# Revit family: SENTINEL KINETIC PLUS_130510_Vent-Axia
name_source: partatom
category: Mechanical Equipment
revit_build: Autodesk Revit MEP 2013 (Build: 20120221_2030(x64)
units: mm (PartAtom-declared; Revit-internal decimal feet)

## types (1)
- Kinetic- B
    A = • Manufactured in the UK, • Building Regulations Part F compliant
    AC Frequency Input = 50Hz nominal
    AC Voltage Input = 220-240 V AC (single phase)
    Air Intake Temperature = (-20C to +45C)
    B = • SAP Appendix Q Eligible, • Energy savings trust best practice compliant
    C = • Up to 92% heat recovery whilst controlling condensation  Unique folding filter for removal when access is restricted
    Category = Sentinel Kinetic
    Cell Clearance = 430 mm
    Condensate Pipe Diameter = 22 mm  [stored 0.0721785 ft]
    Consultants Spec. = Operation
The supply and extract ventilation unit shall be as Sentinel Kinetic as manufactured by Vent-Axia and shall be sized as indicated on the drawings and shall be in accordance with the particular specification.
Supply air to the room shall be pre-heated by the extract air via the integrated composite plastic counterflow heat recovery cell. The Sentinel Kinetic shall automatically vary the ventilation rate via EC/DC motors, as it receives signals from one of the optional interconnected sensors. When a signal is received, the fans shall either vary their speed proportionally or on a trickle and boost principle. The unit shall have the facility to commission the supply and extract fans individually via in-built minimum and maximum speed adjustment, or alternative wired remote control unit. The fans themselves shall have independent, infinitely variable speed control.
Unit specification
The unit shall be manufactured with an ABS Outer case construction, and incorporate a reversible core to allow for left or right hand mounting. The unit shall have a high efficiency composite plastic counterflow heat exchanger, supply and extract filters, automatic summer bypass, (B/BH) integral minimum and maximum infinitely variable speed controls with facia mounted failure indication. The unit shall have low energy, high efficiency EC/DC fan/motor assemblies with sealed for life bearings. The impellers shall be high efficiency forward curved centrifugal type.
The unit shall have a heat exchanger cell with a thermal efficiency of up to 92% when tested to EN 308. This shall be protected by G3 grade synthetic filters on supply and extract. Complete with a condensate drip tray and drain connection. The unit shall be constructed with a removable Core allowing full maintenance access. The removable Core shall provide access to the following:
    Country of Manufacture = UK
    D = • Left or right hand installation ,
    Depth = 526 mm  [stored 1.72572 ft]
    E = • Horizontal and/or vertical duct outlets
    F = • Integrated digital controller for simple and accurate commissioning
    Family = Kinetic
    Filter Clearance = 475 mm  [stored 1.5584 ft]
    G = • Light weight for easy installation, • External condensate connection
    H = • Plug and play controls; Humidistat, Vent-Wise, Wireless remote, • BMS connectivity
    Height (excluding spigots) = 630 mm  [stored 2.06693 ft]
    Height (including Spigots) = 722 mm  [stored 2.36877 ft]
    I = • LS inputs. (Light switch), • Volt-free inputs, • Self diagnosis for simplified fault finding
    IP Rating = IP22
    Install = 600mmx300mmx290mm deep Kitchen Cupboard or loft
    J = • Adjustable delay on/delay off timer
    K = • Easy access G3 filters
    Kitchen + 1 additional wet room = Specific Fan Power (W/l/s)- 0.56 , Thermal Efficiency- 92%
    Kitchen + 2 additional wet room = Specific Fan Power (W/l/s)- 0.49 , Thermal Efficiency- 92%
    Kitchen + 3 additional wet room = Specific Fan Power (W/l/s)- 0.52 , Thermal Efficiency- 91%
    Kitchen + 4 additional wet rooms = Specific Fan Power (W/l/s)- 0.57 , Thermal Efficiency- 90%
    Kitchen + 5 additional wet room = Specific Fan Power (W/l/s)- 0.62 , Thermal Efficiency- 90%
    Kitchen + 6 additional wet room = Specific Fan Power (W/l/s)- 0.7, Thermal Efficiency- 89%
    Kitchen + 7 additional wet room = Specific Fan Power (W/l/s)- 0.8 , Thermal Efficiency- 89%
    Manufacturer - Name = Vent-Axia Ltd
    Manufacturer - Website = www.vent-axia.com
    Motor Rating = 150 W (max)
    Operating Humidity = 0% to 95% RH
    Operating Temperature = (-20C to +45C)
    Operational and Maintenance Manual = www.vent-axia.com/product/clone-sentinel-kinetic-b.html
    Part Number = 443028
    Performance Data = Refer to tab Sentinel Kinetic B, V, BH
    Product Description = Lo-Carbon Kinetic Plus B with summer by-pass and intergal humidity sensor
    SAP Appendix Q Performance = Supply air to the room shall be pre-heated by the extract air via the integrated composite plastic counterflow heat recovery cell. The Sentinel Kinetic shall automatically vary the ventilation rate via EC/DC motors, as it receives signals from one of the optional interconnected sensors. When a signal is received, the fans shall either vary their speed proportionally or on a trickle and boost principle. The unit shall have the facility to commission the supply and extract fans individually via in-built minimum and maximum speed adjustment, or alternative wired remote control unit. The fans themselves shall have independent, infinitely variable speed control.
    Spares (Filters) = Spare Filters (2 pack) - 443351, F5 Pollen Filter - 444201
    Spigot Diameter = 150 mm
    Storage Humidity = 0% to 95% RH
    Storage Temerature = (-20C to +45C)
    Sub Type = B
    Warranty period = Unit 2 years                                    Motor 5 years
    Weight (Kg) = 24 mm  [stored 0.0787402 ft]
    Width (excluding Spigots) = 785 mm

note: [stored X ft] marks values corroborated as IEEE doubles in the binary element streams (Revit-internal decimal feet)

## geometry (parser evidence)
native form markers: Blend x12, Sweep x4
no freeform markers — native parametric forms only
